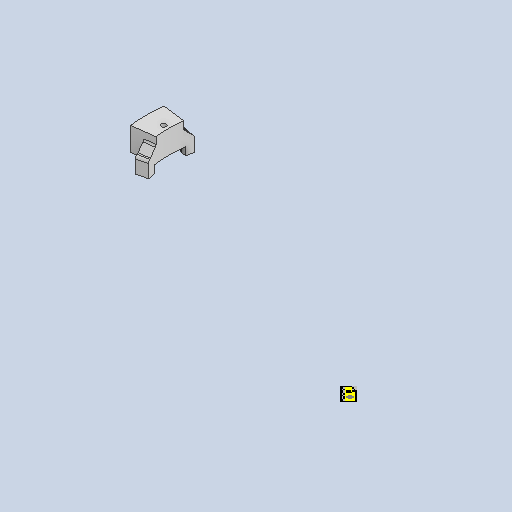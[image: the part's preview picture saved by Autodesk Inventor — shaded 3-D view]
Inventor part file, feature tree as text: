
AUTODESK INVENTOR PART (.ipt)
format: ipt  version: 2025.1 (Build 291241020, 241B)  size: 176,128 bytes
history: native  units: in
note: dims shown in document units (in); Inventor stores cm internally (conversion verified against a paired STEP export)
features: extrude x3, fillet x2, sketch x1, chamfer x1
ambient origin geometry x8: Origin, YZ Plane, XZ Plane, XY Plane, X Axis, Y Axis, Z Axis, Center Point
bodies: Solid1 (feature_tree)
feature tree (7):
  sketch  "Sketch1"  dims[d0=0.209in d1=1.0in d2=1.0in d3=0.0in d4=9.5in d5=10.0in d6=7.25in d7=0.0515in d8=0.0515in d9=0.22in d10=11.0in d11=4.53in d12=14.0in d13=0.1718in d14=0.0859in d15=0.67in d16=0.0in d17=0.33in d18=0.125in d19=45.0deg d20=0.125in d21=0.25in d22=0.1168in d23=0.0584in d24=0.335in d25=0.0in]
  extrude  "Extrusion1"  Depth=0.25in
  extrude  "Extrusion2"  Depth=0.25in TaperAngle=0.0deg
  extrude  "Extrusion3"  Depth=0.25in
  chamfer  "Chamfer1"  Distance=10.0in
  fillet  "Fillet1"  Radius=7.25in
  fillet  "Fillet2"  Radius=0.0515in
